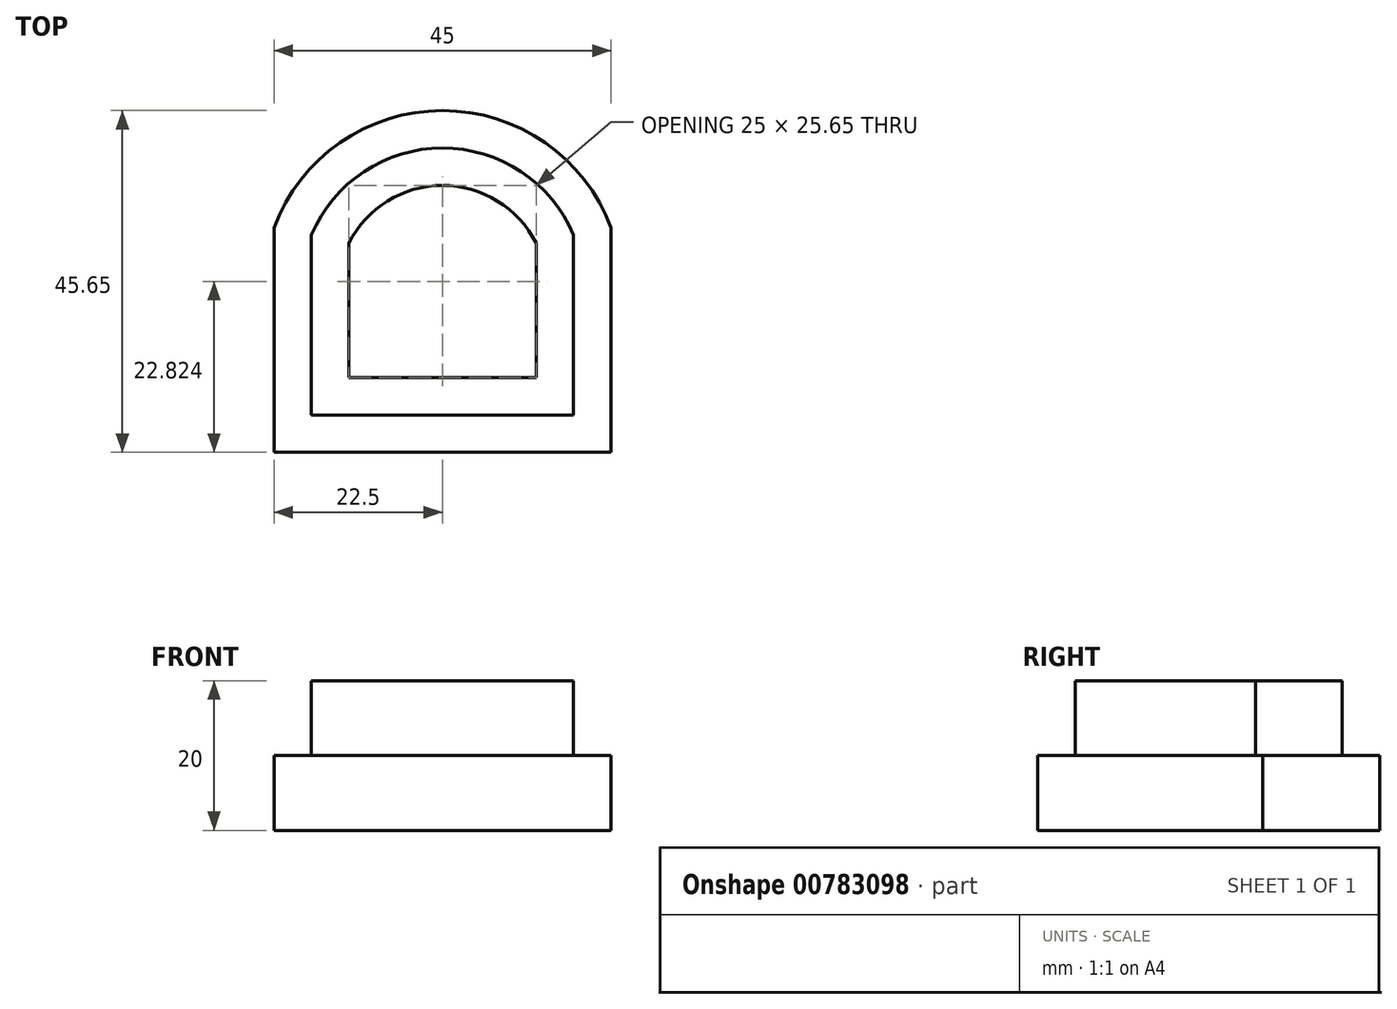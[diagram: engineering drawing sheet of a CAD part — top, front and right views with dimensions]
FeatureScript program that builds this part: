
annotation { "Feature Type Name" : "Feature", "Feature Type Description" : "" }
export const myFeature = defineFeature(function(context is Context, id is Id, definition is map)
    precondition{}
    {
        {
            var Q0;
            Q0=qCreatedBy(makeId("Top.planeOp"),FACE);
            var sketch = newSketch(context, id + "F0", { "sketchPlane" : qUnion([Q0])});
            skLineSegment(sketch, "E0.bottom", {"start": v(0, 0) * mm, "end": v(45, 0) * mm});
            skLineSegment(sketch, "E0.top", {"start": v(0, 30) * mm, "end": v(45, 30) * mm});
            skLineSegment(sketch, "E0.left", {"start": v(0, 0) * mm, "end": v(0, 30) * mm});
            skLineSegment(sketch, "E0.right", {"start": v(45, 0) * mm, "end": v(45, 30) * mm});
            skArc(sketch, "E1", {"start": v(45, 30) * mm, "mid": v(22.5, 45.65) * mm, "end": v(0, 30) * mm});
            skSolve(sketch);
        }
        {
            var Q0;
            Q0=makeQuery(id+"F0.imprint","IMPRINT",FACE,{"disambiguationData":[TD([[makeQuery(id+"F0.imprint","IMPRINT",EDGE,{"derivedFrom":sQuery(id+"F0.wireOp",EDGE,"E0.bottom")}),1.0]])]});
            var Q1;
            Q1=makeQuery(id+"F0.imprint","IMPRINT",FACE,{"disambiguationData":[TD([[makeQuery(id+"F0.imprint","IMPRINT",EDGE,{"derivedFrom":sQuery(id+"F0.wireOp",EDGE,"E0.top")}),1.0]])]});
            extrude(context, id + "F1", {"entities" : qUnion([Q0, Q1]), "depth" : 10 * mm, "offsetDistance" : 25 * mm});
        }
        {
            var Q0;
            Q0=makeQuery(id+"F1.opExtrude","CAP_FACE",FACE,{"disambiguationData":[OSD([sQuery(id+"F0.wireOp",EDGE,"E0.bottom"),sQuery(id+"F0.wireOp",EDGE,"E0.left"),sQuery(id+"F0.wireOp",EDGE,"E0.right"),sQuery(id+"F0.wireOp",EDGE,"E1")])],"isStart":false});
            var sketch = newSketch(context, id + "F2", { "sketchPlane" : qUnion([Q0])});
            skLineSegment(sketch, "E2.0", {"start": v(40, 5) * mm, "end": v(40, 29.05) * mm});
            skLineSegment(sketch, "E2.1", {"start": v(5, 5) * mm, "end": v(40, 5) * mm});
            skLineSegment(sketch, "E2.2", {"start": v(5, 5) * mm, "end": v(5, 29.05) * mm});
            skArc(sketch, "E2.3", {"start": v(40, 29.05) * mm, "mid": v(22.5, 40.65) * mm, "end": v(5, 29.05) * mm});
            skSolve(sketch);
        }
        {
            var Q0;
            Q0=makeQuery(id+"F2.imprint","IMPRINT",FACE,{"disambiguationData":[TD([[makeQuery(id+"F2.imprint","IMPRINT",EDGE,{"derivedFrom":sQuery(id+"F2.wireOp",EDGE,"E2.0")}),1.0]])]});
            extrude(context, id + "F3", {"entities" : qUnion([Q0]), "operationType" : NewBodyOperationType.ADD, "depth" : 10 * mm, "offsetDistance" : 25 * mm});
        }
        {
            var Q0;
            Q0=makeQuery(id+"F3.opExtrude","CAP_FACE",FACE,{"disambiguationData":[OSD([sQuery(id+"F2.wireOp",EDGE,"E2.0"),sQuery(id+"F2.wireOp",EDGE,"E2.1"),sQuery(id+"F2.wireOp",EDGE,"E2.2"),sQuery(id+"F2.wireOp",EDGE,"E2.3")])],"isStart":false});
            var sketch = newSketch(context, id + "F4", { "sketchPlane" : qUnion([Q0])});
            skLineSegment(sketch, "E3.0", {"start": v(10, 10) * mm, "end": v(10, 27.95) * mm});
            skLineSegment(sketch, "E3.1", {"start": v(10, 10) * mm, "end": v(35, 10) * mm});
            skLineSegment(sketch, "E3.2", {"start": v(35, 10) * mm, "end": v(35, 27.95) * mm});
            skArc(sketch, "E3.3", {"start": v(35, 27.95) * mm, "mid": v(22.5, 35.65) * mm, "end": v(10, 27.95) * mm});
            skSolve(sketch);
        }
        {
            var Q0;
            Q0 = qSketchRegion(id + "F4", true);
            extrude(context, id + "F5", {"entities" : qUnion([Q0]), "operationType" : NewBodyOperationType.REMOVE, "oppositeDirection" : true, "depth" : 20 * mm, "offsetDistance" : 25 * mm});
        }
    });
